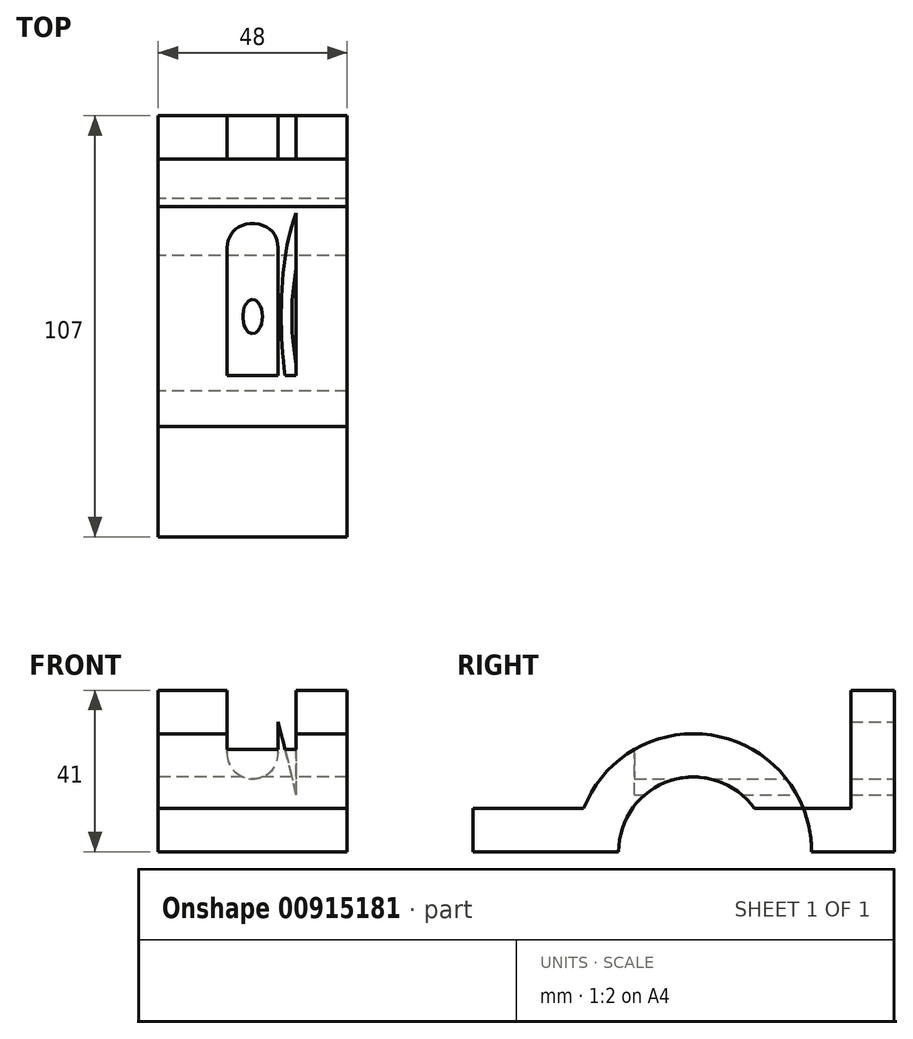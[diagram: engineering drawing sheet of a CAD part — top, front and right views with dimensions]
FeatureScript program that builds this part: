
annotation { "Feature Type Name" : "Feature", "Feature Type Description" : "" }
export const myFeature = defineFeature(function(context is Context, id is Id, definition is map)
    precondition{}
    {
        {
            var Q0;
            Q0=qCreatedBy(makeId("Right.planeOp"),FACE);
            var sketch = newSketch(context, id + "F0", { "sketchPlane" : qUnion([Q0])});
            skCircle(sketch, "E0", {"center": v(0, 0) * mm, "radius": 19 * mm});
            skCircle(sketch, "E1", {"center": v(0, 0) * mm, "radius": 30 * mm});
            skLineSegment(sketch, "E2.bottom", {"start": v(-56, 0) * mm, "end": v(51, 0) * mm});
            skLineSegment(sketch, "E2.top", {"start": v(-56, 11) * mm, "end": v(51, 11) * mm});
            skLineSegment(sketch, "E2.left", {"start": v(-56, 0) * mm, "end": v(-56, 11) * mm});
            skLineSegment(sketch, "E2.right", {"start": v(51, 0) * mm, "end": v(51, 11) * mm});
            skLineSegment(sketch, "E3.top", {"start": v(51, 41) * mm, "end": v(40, 41) * mm});
            skLineSegment(sketch, "E3.left", {"start": v(51, 11) * mm, "end": v(51, 41) * mm});
            skLineSegment(sketch, "E3.right", {"start": v(40, 11) * mm, "end": v(40, 41) * mm});
            skSolve(sketch);
        }
        {
            var Q0;
            {var subQ0=sQuery(id+"F0.wireOp",EDGE,"E2.top");var subQ1=sQuery(id+"F0.wireOp",EDGE,"E0");var subQ2=makeQuery(id+"F0.imprint","INTERSECT",VERTEX,{"disambiguationData":[OD(0.0)],"derivedFrom":[subQ1,subQ0]});Q0=makeQuery(id+"F0.imprint","IMPRINT",FACE,{"disambiguationData":[TD([[makeQuery(id+"F0.imprint","IMPRINT",EDGE,{"disambiguationData":[TD([[subQ2,-1.0]])],"derivedFrom":subQ1}),-1.0]])]});}
            var Q1;
            {var subQ0=sQuery(id+"F0.wireOp",EDGE,"E2.right");Q1=makeQuery(id+"F0.imprint","IMPRINT",FACE,{"disambiguationData":[TD([[makeQuery(id+"F0.imprint","IMPRINT",EDGE,{"derivedFrom":subQ0}),1.0]])]});}
            var Q2;
            {var subQ0=sQuery(id+"F0.wireOp",EDGE,"E2.top");var subQ1=sQuery(id+"F0.wireOp",EDGE,"E0");var subQ2=makeQuery(id+"F0.imprint","INTERSECT",VERTEX,{"disambiguationData":[OD(0.0)],"derivedFrom":[subQ1,subQ0]});Q2=makeQuery(id+"F0.imprint","IMPRINT",FACE,{"disambiguationData":[TD([[makeQuery(id+"F0.imprint","IMPRINT",EDGE,{"disambiguationData":[TD([[subQ2,1.0]])],"derivedFrom":subQ1}),-1.0]])]});}
            var Q3;
            Q3=makeQuery(id+"F0.imprint","IMPRINT",FACE,{"disambiguationData":[TD([[makeQuery(id+"F0.imprint","IMPRINT",EDGE,{"derivedFrom":sQuery(id+"F0.wireOp",EDGE,"E3.top")}),1.0]])]});
            var Q4;
            {var subQ5=sQuery(id+"F0.wireOp",EDGE,"E2.left");Q4=makeQuery(id+"F0.imprint","IMPRINT",FACE,{"disambiguationData":[TD([[makeQuery(id+"F0.imprint","IMPRINT",EDGE,{"derivedFrom":subQ5}),-1.0]])]});}
            var Q5;
            {var subQ0=sQuery(id+"F0.wireOp",EDGE,"E2.top");var subQ1=sQuery(id+"F0.wireOp",EDGE,"E0");var subQ2=makeQuery(id+"F0.imprint","INTERSECT",VERTEX,{"disambiguationData":[OD(1.0)],"derivedFrom":[subQ1,subQ0]});Q5=makeQuery(id+"F0.imprint","IMPRINT",FACE,{"disambiguationData":[TD([[makeQuery(id+"F0.imprint","IMPRINT",EDGE,{"disambiguationData":[TD([[subQ2,-1.0]])],"derivedFrom":subQ1}),-1.0]])]});}
            extrude(context, id + "F1", {"entities" : qUnion([Q0, Q1, Q2, Q3, Q4, Q5]), "endBound" : BoundingType.SYMMETRIC, "depth" : 48 * mm, "offsetDistance" : 25 * mm});
        }
        {
            var Q0;
            Q0=makeQuery(id+"F1.opExtrude","SWEPT_FACE",FACE,{"disambiguationData":[OSD([sQuery(id+"F0.wireOp",EDGE,"E2.right"),sQuery(id+"F0.wireOp",EDGE,"E3.left")])]});
            var sketch = newSketch(context, id + "F2", { "sketchPlane" : qUnion([Q0])});
            skLineSegment(sketch, "E4", {"start": v(0, 0) * mm, "end": v(0, 41) * mm, "construction": true});
            skCircle(sketch, "E5", {"center": v(0, 25) * mm, "radius": 6.5 * mm});
            skLineSegment(sketch, "E6", {"start": v(-6.5, 25) * mm, "end": v(-6.5, 41) * mm});
            skLineSegment(sketch, "E7", {"start": v(6.5, 25) * mm, "end": v(6.5, 41) * mm});
            skLineSegment(sketch, "E8", {"start": v(-11.08, 41) * mm, "end": v(-11.08, 14.51) * mm});
            skLineSegment(sketch, "E9", {"start": v(-11.08, 14.51) * mm, "end": v(-6.5, 33) * mm});
            skLineSegment(sketch, "E10", {"start": v(-11.08, 41) * mm, "end": v(-6.5, 41) * mm});
            skSolve(sketch);
        }
        {
            var Q0;
            {var subQ0=sQuery(id+"F2.wireOp",EDGE,"E5");var subQ2=makeQuery(id+"F2.imprint","INTERSECT",VERTEX,{"derivedFrom":[subQ0,sQuery(id+"F2.wireOp",EDGE,"E6")]});Q0=makeQuery(id+"F2.imprint","IMPRINT",FACE,{"disambiguationData":[TD([[makeQuery(id+"F2.imprint","IMPRINT",EDGE,{"disambiguationData":[TD([[subQ2,1.0]])],"derivedFrom":subQ0}),1.0]])]});}
            var Q1;
            Q1=makeQuery(id+"F2.imprint","IMPRINT",FACE,{"disambiguationData":[TD([[makeQuery(id+"F2.imprint","IMPRINT",EDGE,{"derivedFrom":sQuery(id+"F2.wireOp",EDGE,"E8")}),1.0]])]});
            var Q2;
            {var subQ0=sQuery(id+"F2.wireOp",EDGE,"E7");Q2=makeQuery(id+"F2.imprint","IMPRINT",FACE,{"disambiguationData":[TD([[makeQuery(id+"F2.imprint","IMPRINT",EDGE,{"derivedFrom":subQ0}),1.0]])]});}
            var Q3;
            Q3=makeQuery(id+"F1.opExtrude","SWEPT_FACE",FACE,{"disambiguationData":[OSD([sQuery(id+"F0.wireOp",EDGE,"E3.right")])]});
            extrude(context, id + "F3", {"entities" : qUnion([Q0, Q1, Q2]), "operationType" : NewBodyOperationType.REMOVE, "endBound" : BoundingType.UP_TO_SURFACE, "oppositeDirection" : true, "endBoundEntityFace" : qUnion([Q3]), "hasOffset" : true, "offsetDistance" : -55 * mm, "depth" : 25 * mm});
        }
    });
